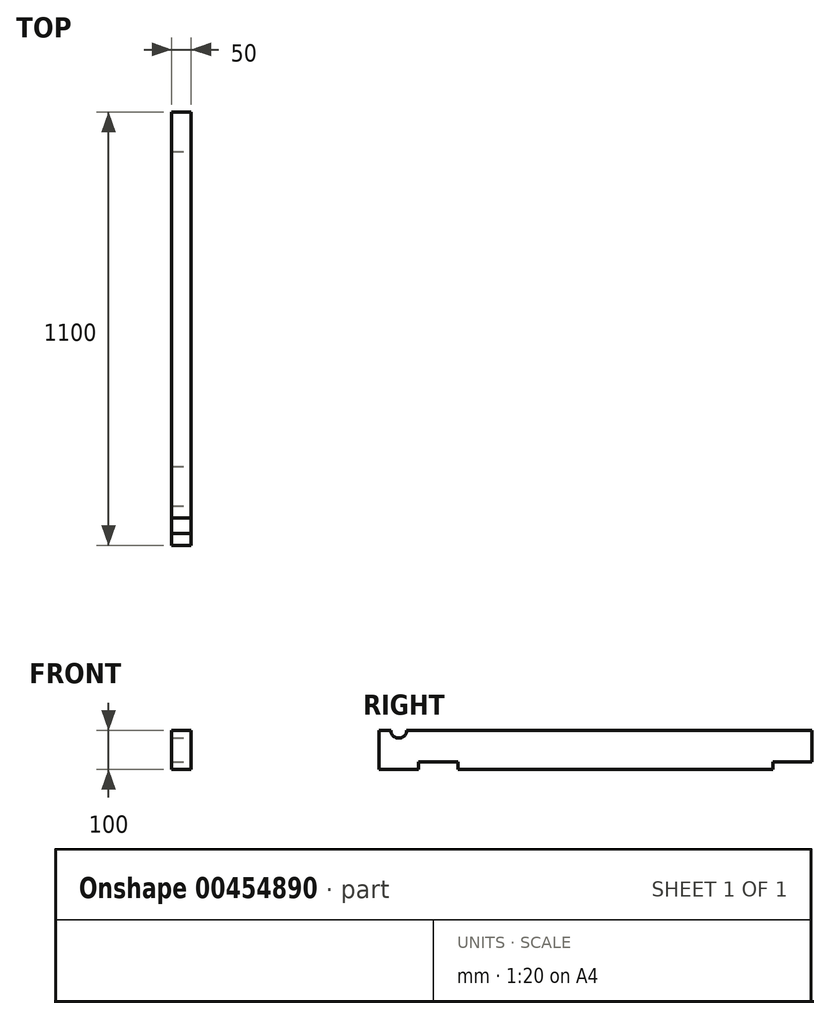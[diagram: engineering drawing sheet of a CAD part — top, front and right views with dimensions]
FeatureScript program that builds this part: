
annotation { "Feature Type Name" : "Feature", "Feature Type Description" : "" }
export const myFeature = defineFeature(function(context is Context, id is Id, definition is map)
    precondition{}
    {
        {
            var Q0;
            Q0=qCreatedBy(makeId("Front.planeOp"),FACE);
            var sketch = newSketch(context, id + "F0", { "sketchPlane" : qUnion([Q0])});
            skLineSegment(sketch, "E0.bottom", {"start": v(0, 0) * mm, "end": v(50, 0) * mm});
            skLineSegment(sketch, "E0.top", {"start": v(0, 100) * mm, "end": v(50, 100) * mm});
            skLineSegment(sketch, "E0.left", {"start": v(0, 0) * mm, "end": v(0, 100) * mm});
            skLineSegment(sketch, "E0.right", {"start": v(50, 0) * mm, "end": v(50, 100) * mm});
            skSolve(sketch);
        }
        {
            var Q0;
            Q0 = qSketchRegion(id + "F0", true);
            extrude(context, id + "F1", {"entities" : qUnion([Q0]), "depth" : 1100 * mm});
        }
        {
            var Q0;
            Q0=makeQuery(id+"F1.opExtrude","SWEPT_FACE",FACE,{"disambiguationData":[OSD([sQuery(id+"F0.wireOp",EDGE,"E0.right")])]});
            var sketch = newSketch(context, id + "F2", { "sketchPlane" : qUnion([Q0])});
            skLineSegment(sketch, "E1.bottom", {"start": v(0, 0) * mm, "end": v(-100, 0) * mm});
            skLineSegment(sketch, "E1.top", {"start": v(0, 20) * mm, "end": v(-100, 20) * mm});
            skLineSegment(sketch, "E1.left", {"start": v(0, 0) * mm, "end": v(0, 20) * mm});
            skLineSegment(sketch, "E1.right", {"start": v(-100, 0) * mm, "end": v(-100, 20) * mm});
            skLineSegment(sketch, "E2.bottom", {"start": v(-900, 0) * mm, "end": v(-1000, 0) * mm});
            skLineSegment(sketch, "E2.top", {"start": v(-900, 20) * mm, "end": v(-1000, 20) * mm});
            skLineSegment(sketch, "E2.left", {"start": v(-1000, 0) * mm, "end": v(-1000, 20) * mm});
            skLineSegment(sketch, "E2.right", {"start": v(-900, 0) * mm, "end": v(-900, 20) * mm});
            skSolve(sketch);
        }
        {
            var Q0;
            Q0 = qSketchRegion(id + "F2", true);
            extrude(context, id + "F3", {"entities" : qUnion([Q0]), "operationType" : NewBodyOperationType.REMOVE, "endBound" : BoundingType.THROUGH_ALL, "oppositeDirection" : true, "depth" : 25 * mm});
        }
        {
            var Q0;
            Q0=makeQuery(id+"F1.opExtrude","SWEPT_FACE",FACE,{"disambiguationData":[OSD([sQuery(id+"F0.wireOp",EDGE,"E0.right")])]});
            var sketch = newSketch(context, id + "F4", { "sketchPlane" : qUnion([Q0])});
            skArc(sketch, "E3", {"start": v(-1070, 100) * mm, "mid": v(-1050, 80) * mm, "end": v(-1030, 100) * mm});
            skLineSegment(sketch, "E4", {"start": v(-1070, 100) * mm, "end": v(-1030, 100) * mm});
            skSolve(sketch);
        }
        {
            var Q0;
            Q0 = qSketchRegion(id + "F4", true);
            extrude(context, id + "F5", {"entities" : qUnion([Q0]), "operationType" : NewBodyOperationType.REMOVE, "endBound" : BoundingType.THROUGH_ALL, "oppositeDirection" : true, "depth" : 25 * mm});
        }
    });
